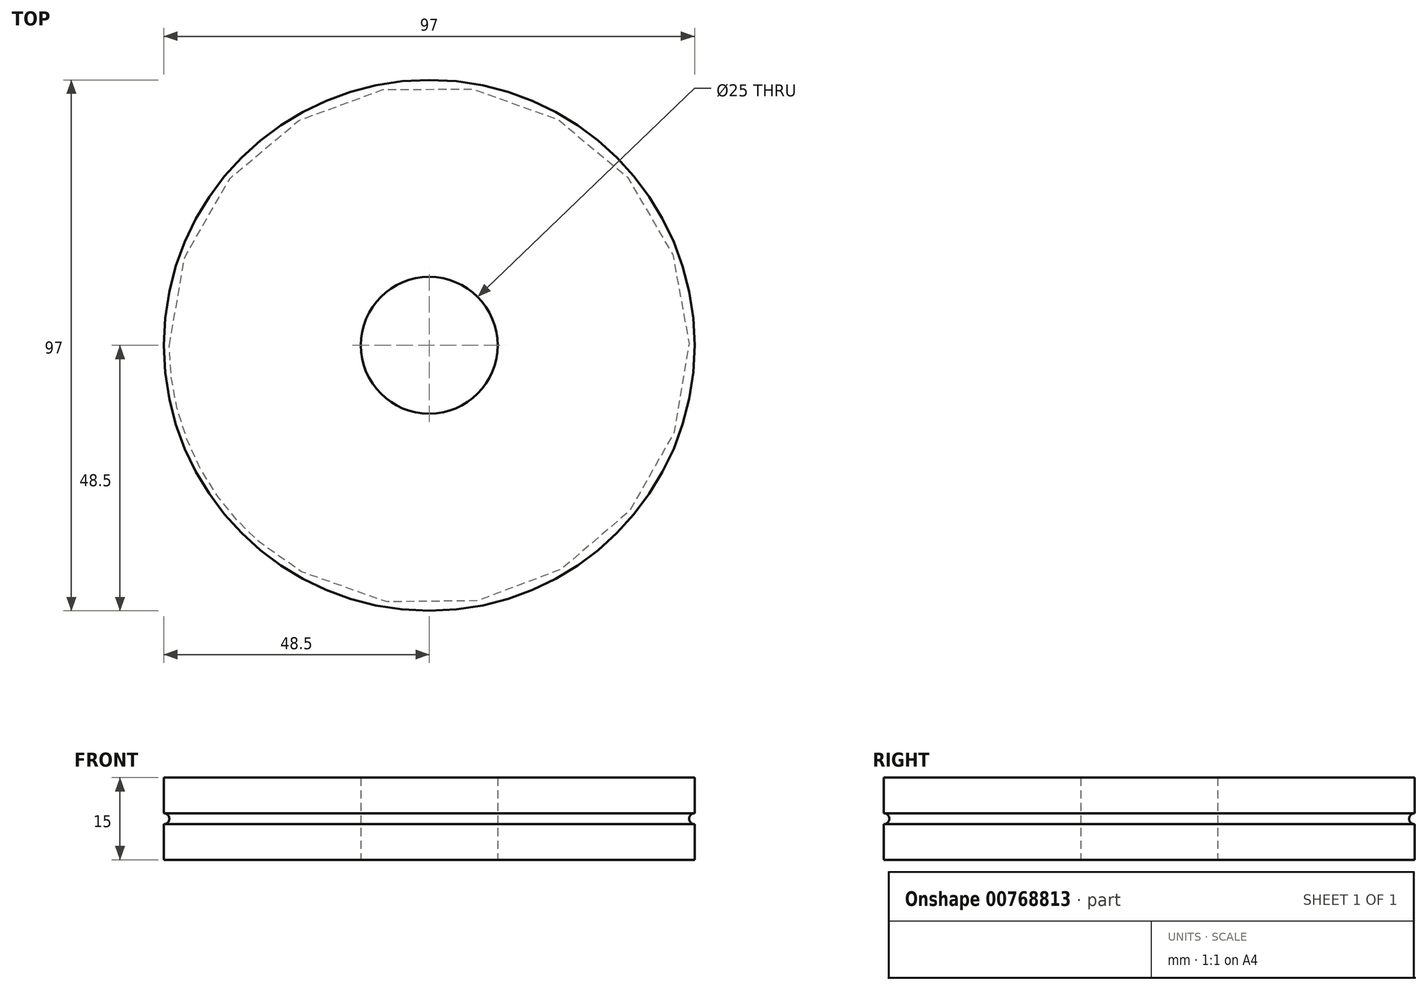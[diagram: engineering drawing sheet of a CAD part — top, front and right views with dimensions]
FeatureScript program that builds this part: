
annotation { "Feature Type Name" : "Feature", "Feature Type Description" : "" }
export const myFeature = defineFeature(function(context is Context, id is Id, definition is map)
    precondition{}
    {
        {
            var Q0;
            Q0=qCreatedBy(makeId("Top.planeOp"),FACE);
            var sketch = newSketch(context, id + "F0", { "sketchPlane" : qUnion([Q0])});
            skCircle(sketch, "E0", {"center": v(0, 0) * mm, "radius": 48.5 * mm});
            skSolve(sketch);
        }
        {
            var Q0;
            Q0=makeQuery(id+"F0.imprint","IMPRINT",FACE,{"disambiguationData":[TD([[makeQuery(id+"F0.imprint","IMPRINT",EDGE,{"derivedFrom":sQuery(id+"F0.wireOp",EDGE,"E0")}),1.0]])]});
            var sketch = newSketch(context, id + "F1", { "sketchPlane" : qUnion([Q0])});
            skSolve(sketch);
        }
        {
            var Q0;
            Q0=makeQuery(id+"F1.imprint","IMPRINT",FACE,{"disambiguationData":[TD([[makeQuery(id+"F1.imprint","IMPRINT",EDGE,{"derivedFrom":makeQuery(id+"F0.imprint","IMPRINT",EDGE,{"derivedFrom":sQuery(id+"F0.wireOp",EDGE,"E0")})}),1.0]])]});
            extrude(context, id + "F2", {"entities" : qUnion([Q0]), "depth" : 15 * mm, "offsetDistance" : 25 * mm});
        }
        {
            var Q0;
            Q0=qCreatedBy(makeId("Front.planeOp"),FACE);
            var sketch = newSketch(context, id + "F3", { "sketchPlane" : qUnion([Q0])});
            skLineSegment(sketch, "E1", {"start": v(0, 7.5) * mm, "end": v(0, 0) * mm});
            skLineSegment(sketch, "E2", {"start": v(0, 7.5) * mm, "end": v(48.5, 7.5) * mm});
            skCircle(sketch, "E3", {"center": v(48.5, 7.5) * mm, "radius": 1 * mm});
            skLineSegment(sketch, "E4", {"start": v(0, 0) * mm, "end": v(0, 16.75) * mm});
            skSolve(sketch);
        }
        {
            var Q0;
            Q0=makeQuery(id+"F3.imprint","IMPRINT",FACE,{"disambiguationData":[TD([[makeQuery(id+"F3.imprint","IMPRINT",EDGE,{"derivedFrom":sQuery(id+"F3.wireOp",EDGE,"E3")}),1.0]])]});
            var Q1;
            Q1=sQuery(id+"F3.wireOp",EDGE,"E3");
            var Q2;
            Q2=sQuery(id+"F3.wireOp",EDGE,"E4");
            revolve(context, id + "F4", {"operationType" : NewBodyOperationType.REMOVE, "surfaceOperationType" : NewSurfaceOperationType.NEW, "entities" : qUnion([Q0]), "surfaceEntities" : qUnion([Q1]), "axis" : qUnion([Q2]), "revolveType" : RevolveType.FULL});
        }
        {
            var Q0;
            Q0=qCreatedBy(makeId("Top.planeOp"),FACE);
            var sketch = newSketch(context, id + "F5", { "sketchPlane" : qUnion([Q0])});
            skCircle(sketch, "E5", {"center": v(0, 0) * mm, "radius": 12.5 * mm});
            skSolve(sketch);
        }
        {
            var Q0;
            Q0=makeQuery(id+"F5.imprint","IMPRINT",FACE,{"disambiguationData":[TD([[makeQuery(id+"F5.imprint","IMPRINT",EDGE,{"derivedFrom":sQuery(id+"F5.wireOp",EDGE,"E5")}),1.0]])]});
            extrude(context, id + "F6", {"entities" : qUnion([Q0]), "operationType" : NewBodyOperationType.REMOVE, "depth" : 15 * mm, "offsetDistance" : 25 * mm});
        }
    });
